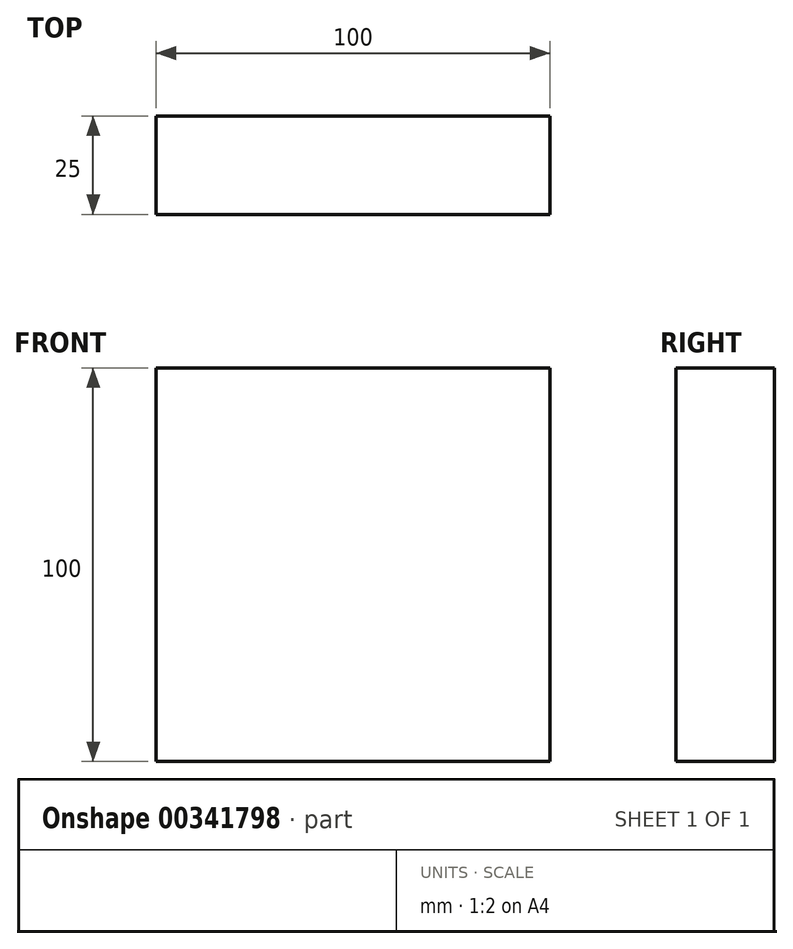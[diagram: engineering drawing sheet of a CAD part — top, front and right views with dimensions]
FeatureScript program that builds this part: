
annotation { "Feature Type Name" : "Feature", "Feature Type Description" : "" }
export const myFeature = defineFeature(function(context is Context, id is Id, definition is map)
    precondition{}
    {
        {
            var Q0;
            Q0=qCreatedBy(makeId("Front.planeOp"),FACE);
            var sketch = newSketch(context, id + "F0", { "sketchPlane" : qUnion([Q0])});
            skLineSegment(sketch, "E0.bottom", {"start": v(0, 0) * mm, "end": v(100, 0) * mm});
            skLineSegment(sketch, "E0.top", {"start": v(0, 100) * mm, "end": v(100, 100) * mm});
            skLineSegment(sketch, "E0.left", {"start": v(0, 0) * mm, "end": v(0, 100) * mm});
            skLineSegment(sketch, "E0.right", {"start": v(100, 0) * mm, "end": v(100, 100) * mm});
            skSolve(sketch);
        }
        {
            var Q0;
            Q0=makeQuery(id+"F0.imprint","IMPRINT",FACE,{"disambiguationData":[TD([[makeQuery(id+"F0.imprint","IMPRINT",EDGE,{"derivedFrom":sQuery(id+"F0.wireOp",EDGE,"E0.bottom")}),1.0]])]});
            extrude(context, id + "F1", {"entities" : qUnion([Q0]), "depth" : 25 * mm});
        }
    });
